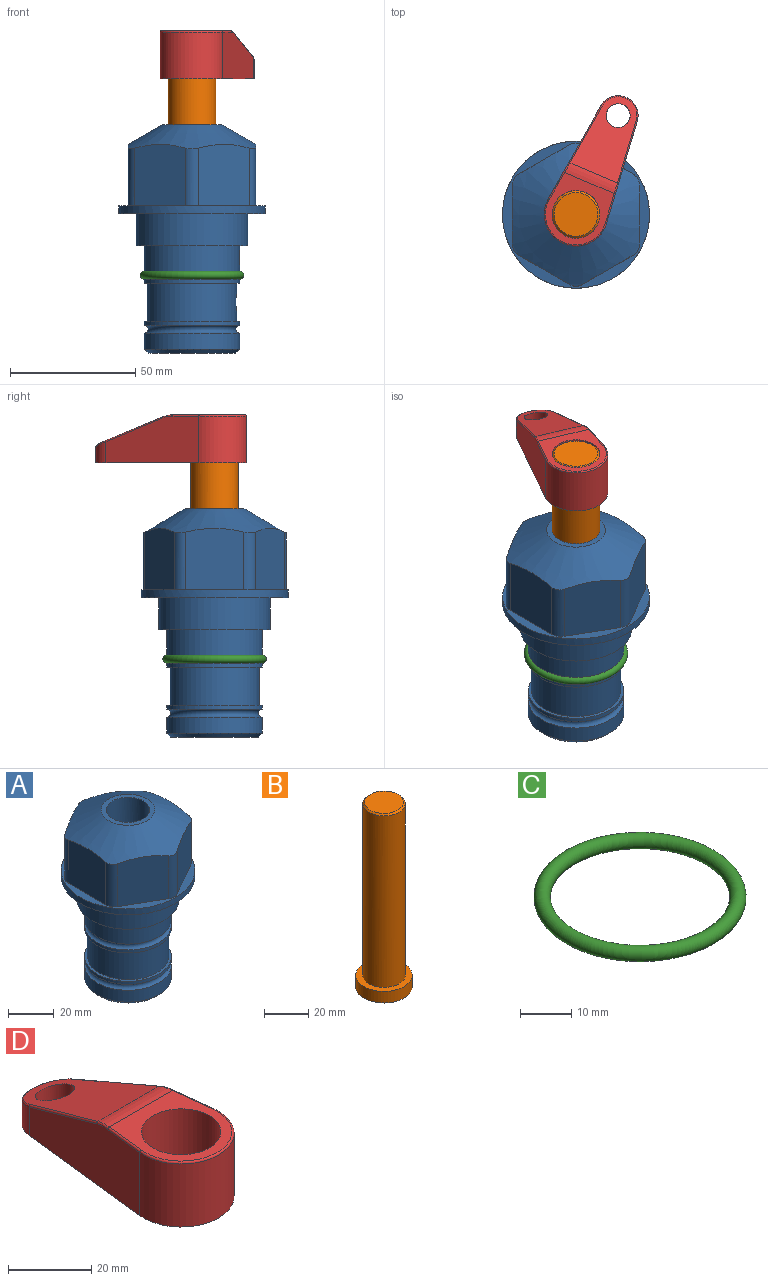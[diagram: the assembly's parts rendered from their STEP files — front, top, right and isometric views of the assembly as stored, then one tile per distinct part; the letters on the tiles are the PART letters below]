
ASSEMBLY  parts=4 mates=2
PART A: 36 faces, bbox 58.7x58.7x91.2 mm
  f0: cylinder r=17.78mm len=35.56mm, axis (0,0,1), area 1670.8mm2, adj f23,f24,f31
  f1: cylinder r=19.05mm len=38.1mm, axis (0,0,1), area 1191.9mm2, adj f26,f27,f30
  f2: plane 58.66x58.66mm, normal (0,0,-1), area 1150.6mm2, adj f3,f28
  f3: cylinder r=29.33mm len=58.66mm, axis (0,0,-1), area 585.1mm2, adj f2,f4
  f4: plane 58.66x58.66mm, normal (0,0,1), area 475.9mm2, adj f3,f5,f6,f7,f8,f9,f10,f11
  f5: plane 24.5x20.32mm, normal (-0.5,0.87,0), area 562.8mm2, adj f4,f15,f16,f17
  f6: plane 24.5x20.32mm, normal (0.5,0.87,0), area 562.8mm2, adj f4,f14,f15,f17
  f7: plane 24.5x23.48mm, normal (1,0,0), area 562.8mm2, adj f4,f13,f14,f17
  f8: plane 24.5x20.32mm, normal (0.5,-0.87,0), area 562.8mm2, adj f4,f12,f13,f17
  f9: plane 24.5x20.32mm, normal (-0.5,-0.87,0), area 562.8mm2, adj f4,f11,f12,f17
  f10: plane 24.5x23.48mm, normal (-1,0,0), area 562.8mm2, adj f4,f11,f16,f17
  f11: cylinder r=5.08mm len=23.01mm, axis (0,0,-1), area 121.2mm2, adj f4,f9,f10,f17
  f12: cylinder r=5.08mm len=23.01mm, axis (0,0,-1), area 121.2mm2, adj f4,f8,f9,f17
  f13: cylinder r=5.08mm len=23.01mm, axis (0,0,-1), area 121.2mm2, adj f4,f7,f8,f17
  f14: cylinder r=5.08mm len=23.01mm, axis (0,0,-1), area 121.2mm2, adj f4,f6,f7,f17
  f15: cylinder r=5.08mm len=23.01mm, axis (0,0,-1), area 121.2mm2, adj f4,f5,f6,f17
  f16: cylinder r=5.08mm len=23.01mm, axis (0,0,-1), area 121.2mm2, adj f4,f5,f10,f17
  f17: cone r=11.73mm half-angle=60deg, axis (0,0,-1), area 2071.8mm2, adj f5,f6,f7,f8,f9,f10,f11,f12
  f18: plane 23.46x23.46mm, normal (0,0,1), area 147.4mm2, adj f17,f35
  f19: plane 34.93x34.93mm, normal (0,0,-1), area 958mm2, adj f29
  f20: cylinder r=19.05mm len=38.1mm, axis (0,0,1), area 760.1mm2, adj f21,f29
  f21: torus R=19.05mm, axis (0,0,1), area 565.3mm2, adj f20,f22
  f22: cylinder r=19.05mm len=38.1mm, axis (0,0,1), area 190mm2, adj f21,f23
  f23: plane 38.1x38.1mm, normal (0,0,1), area 146.9mm2, adj f0,f22
  f24: plane 38.1x38.1mm, normal (0,0,-1), area 146.9mm2, adj f0,f25
  f25: cylinder r=19.05mm len=38.1mm, axis (0,0,1), area 190mm2, adj f24,f26
  f26: torus R=19.05mm, axis (0,0,1), area 565.3mm2, adj f1,f25
  f27: plane 44.45x44.45mm, normal (0,0,-1), area 411.7mm2, adj f1,f28
  f28: cylinder r=22.23mm len=44.45mm, axis (0,0,1), area 1773.5mm2, adj f2,f27
  f29: cone r=19.05mm half-angle=45deg, axis (0,0,1), area 257.5mm2, adj f19,f20
  f30: cylinder r=3.17mm len=6.75mm, axis (-1,0,0), area 128mm2, adj f1,f33
  f31: cylinder r=3.17mm len=6.35mm, axis (-1,0,0), area 102.5mm2, adj f0,f33
  f32: plane 25.4x25.4mm, normal (0,0,1), area 506.7mm2, adj f33
  f33: cylinder r=12.7mm len=66.42mm, axis (0,0,-1), area 5236.2mm2, adj f30,f31,f32,f34
  f34: cone r=9.53mm half-angle=30deg, axis (0,0,-1), area 443.4mm2, adj f33,f35
  f35: cylinder r=9.53mm len=19.05mm, axis (0,0,-1), area 849mm2, adj f18,f34
PART B: 6 faces, bbox 25.4x25.4x101.6 mm
  f0: plane 17.46x17.46mm, normal (0,0,1), area 239.5mm2, adj f5
  f1: plane 25.4x25.4mm, normal (0,0,-1), area 506.7mm2, adj f2
  f2: cylinder r=12.7mm len=25.4mm, axis (0,0,1), area 506.7mm2, adj f1,f3
  f3: plane 25.4x25.4mm, normal (0,0,1), area 221.7mm2, adj f2,f4
  f4: cylinder r=9.53mm len=94.46mm, axis (0,0,1), area 5653mm2, adj f3,f5
  f5: cone r=8.73mm half-angle=45deg, axis (0,0,-1), area 64.4mm2, adj f0,f4
PART C: 1 faces, bbox 44.7x44.7x3.2 mm
  f0: torus R=19.05mm, axis (0,0,1), area 1193.9mm2
PART D: 44 faces, bbox 27.5x64.5x19.1 mm
  f0: plane 2.3x0.95mm, normal (0,0,-1), area 1mm2, adj f25,f30,f34
  f1: plane 63.5x25.4mm, normal (0,0,-1), area 561.7mm2, adj f2,f3,f4,f5,f6,f7,f19,f20
  f2: cylinder r=12.7mm len=25.4mm, axis (0,0,-1), area 792.2mm2, adj f1,f3,f5,f13
  f3: plane 42.33x18.54mm, normal (0.99,0.11,0), area 647mm2, adj f1,f2,f4,f11,f12,f14
  f4: cylinder r=7.94mm len=15.78mm, axis (0,0,-1), area 158.6mm2, adj f1,f3,f5,f16
  f5: plane 42.33x18.54mm, normal (-0.99,0.11,0), area 647mm2, adj f1,f2,f4,f15,f17,f18
  f6: cylinder r=9.53mm len=19.05mm, axis (0,0,-1), area 1140.1mm2, adj f1,f8
  f7: cylinder r=4.76mm len=10.98mm, axis (0,0,-1), area 276.1mm2, adj f1,f9
  f8: plane 25.83x24.38mm, normal (0,0,1), area 262.2mm2, adj f6,f10,f11,f13,f15
  f9: plane 32.49x20.55mm, normal (0,0.34,0.94), area 489.9mm2, adj f7,f10,f14,f16,f18
  f10: cylinder r=12.7mm len=21.49mm, axis (-1,0,0), area 93.2mm2, adj f8,f9,f12,f17
  f11: cylinder r=0.51mm len=12.34mm, axis (0.11,-0.99,0), area 9.9mm2, adj f3,f8,f12,f13
  f12: bspline ~7.62x1.64mm, area 3.5mm2, adj f3,f10,f11,f14
  f13: torus R=12.19mm, axis (0,0,1), area 33.6mm2, adj f2,f8,f11,f15
  f14: cylinder r=0.51mm len=26.01mm, axis (0.1,-0.93,0.34), area 21.6mm2, adj f3,f9,f12,f16
  f15: cylinder r=0.51mm len=12.34mm, axis (0.11,0.99,0), area 9.9mm2, adj f5,f8,f13,f17
  f16: bspline ~15.78x7.05mm, area 15.7mm2, adj f4,f9,f14,f18
  f17: bspline ~7.62x1.64mm, area 3.5mm2, adj f5,f10,f15,f18
  f18: cylinder r=0.51mm len=26.01mm, axis (0.1,0.93,-0.34), area 21.6mm2, adj f5,f9,f16,f17
  f19: plane 21.6x14.29mm, normal (-0.99,-0.11,0), area 242.6mm2, adj f1,f26,f28,f34,f36,f38
  f20: plane 21.6x14.29mm, normal (0.99,-0.11,0), area 242.6mm2, adj f1,f27,f29,f37,f39,f41
  f21: cylinder r=12.7mm len=14.29mm, axis (0,0,-1), area 173.2mm2, adj f1,f26,f27,f30,f31,f33
  f22: cylinder r=7.94mm len=7.63mm, axis (0,0,-1), area 53.8mm2, adj f1,f28,f29,f42
  f23: plane 2.3x0.95mm, normal (0,0,-1), area 1mm2, adj f25,f33,f37
  f24: plane 17.94x12.32mm, normal (0,-0.34,-0.94), area 191.2mm2, adj f25,f38,f41,f42
  f25: cylinder r=9.53mm len=12.93mm, axis (-1,0,0), area 37.5mm2, adj f0,f23,f24,f31,f36,f39
  f26: cylinder r=1.59mm len=14.29mm, axis (0,0,-1), area 49mm2, adj f1,f19,f21,f32
  f27: cylinder r=1.59mm len=14.29mm, axis (0,0,-1), area 49mm2, adj f1,f20,f21,f35
  f28: cylinder r=1.59mm len=7.28mm, axis (0,0,-1), area 22.1mm2, adj f1,f19,f22,f40
  f29: cylinder r=1.59mm len=7.28mm, axis (0,0,-1), area 22.1mm2, adj f1,f20,f22,f43
  f30: torus R=14.29mm, axis (0,0,1), area 5.8mm2, adj f0,f21,f31,f32
  f31: bspline ~11.06x2.73mm, area 20.8mm2, adj f21,f25,f30,f33
  f32: sphere r=1.59mm, area 5.4mm2, adj f26,f30,f34
  f33: torus R=14.29mm, axis (0,0,1), area 5.8mm2, adj f21,f23,f31,f35
  f34: cylinder r=1.59mm len=1.68mm, axis (-0.11,0.99,0), area 2.4mm2, adj f0,f19,f32,f36
  f35: sphere r=1.59mm, area 5.4mm2, adj f27,f33,f37
  f36: bspline ~5.82x2.33mm, area 7.7mm2, adj f19,f25,f34,f38
  f37: cylinder r=1.59mm len=1.68mm, axis (0.11,0.99,0), area 2.4mm2, adj f20,f23,f35,f39
  f38: cylinder r=1.59mm len=18.33mm, axis (0.1,-0.93,0.34), area 46.7mm2, adj f19,f24,f36,f40
  f39: bspline ~5.82x2.33mm, area 7.7mm2, adj f20,f25,f37,f41
  f40: sphere r=1.59mm, area 3.6mm2, adj f28,f38,f42
  f41: cylinder r=1.59mm len=18.33mm, axis (0.1,0.93,-0.34), area 46.7mm2, adj f20,f24,f39,f43
  f42: bspline ~8.31x1.84mm, area 15.3mm2, adj f22,f24,f40,f43
  f43: sphere r=1.59mm, area 3.6mm2, adj f29,f41,f42
PLACE A at identity fixed
PLACE B rot(axis=(0,0,-1),23.1deg) t=(0,0,-0.71)mm
PLACE C at identity
PLACE D rot(axis=(0,0,-1),23.1deg) t=(0,0,53.9)mm
MATE fastened D.f2 <-> B.f2  axis (0,0,-1) through (0,0,72.95)mm
MATE cylindrical B.f2 <-> A.f0  axis (0,0,1) through (0,0,24.92)mm
